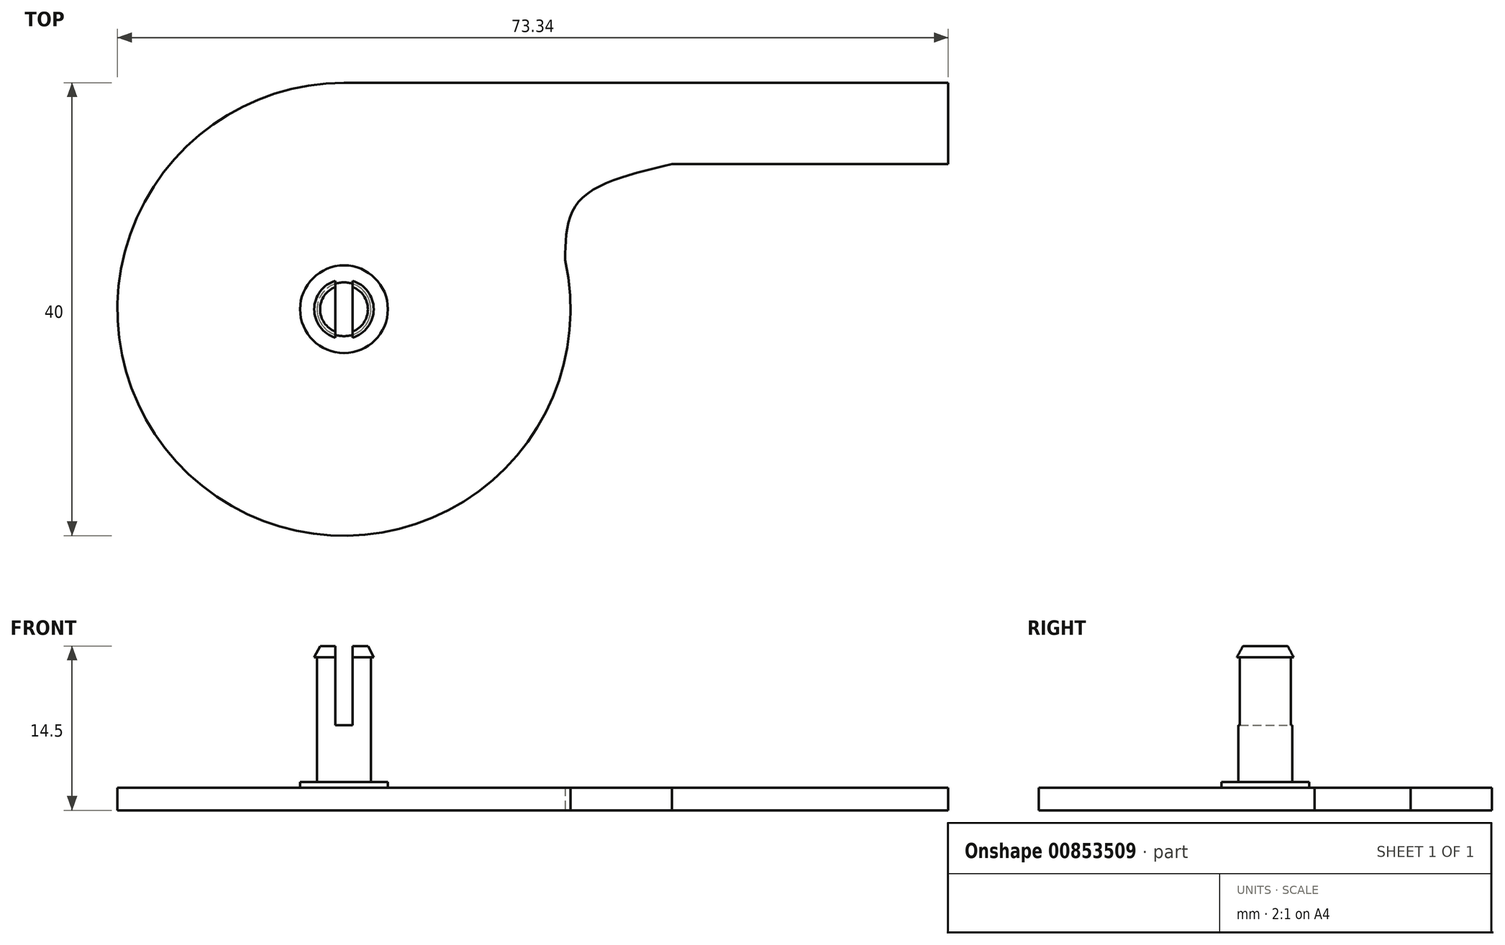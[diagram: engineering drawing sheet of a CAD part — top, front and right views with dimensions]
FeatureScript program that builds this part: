
annotation { "Feature Type Name" : "Feature", "Feature Type Description" : "" }
export const myFeature = defineFeature(function(context is Context, id is Id, definition is map)
    precondition{}
    {
        {
            var Q0;
            Q0=qCreatedBy(makeId("Top.planeOp"),FACE);
            var sketch = newSketch(context, id + "F0", { "sketchPlane" : qUnion([Q0])});
            skCircle(sketch, "E0", {"center": v(0, 0) * mm, "radius": 20 * mm});
            skLineSegment(sketch, "E1", {"start": v(0, 20) * mm, "end": v(53.34, 20) * mm});
            skLineSegment(sketch, "E2", {"start": v(53.34, 20) * mm, "end": v(53.34, 12.82) * mm});
            skLineSegment(sketch, "E3", {"start": v(53.34, 12.82) * mm, "end": v(28.94, 12.82) * mm});
            skFitSpline(sketch, "E4", {"points": [v(19.52, 4.35) * mm, v(20.72, 9.5) * mm, v(28.94, 12.82) * mm], "startDerivative": vector(0.2, 13.14) * mm, "endDerivative": vector(17.92, 4.2) * mm});
            skSolve(sketch);
        }
        {
            var Q0;
            {var subQ0=sQuery(id+"F0.wireOp",EDGE,"E0");var subQ1=makeQuery(id+"F0.imprint","INTERSECT",VERTEX,{"derivedFrom":[subQ0,sQuery(id+"F0.wireOp",EDGE,"E1")]});Q0=makeQuery(id+"F0.imprint","IMPRINT",FACE,{"disambiguationData":[TD([[makeQuery(id+"F0.imprint","IMPRINT",EDGE,{"disambiguationData":[TD([[subQ1,1.0]])],"derivedFrom":subQ0}),1.0]])]});}
            var Q1;
            {var subQ0=sQuery(id+"F0.wireOp",EDGE,"E1");Q1=makeQuery(id+"F0.imprint","IMPRINT",FACE,{"disambiguationData":[TD([[makeQuery(id+"F0.imprint","IMPRINT",EDGE,{"derivedFrom":subQ0}),-1.0]])]});}
            extrude(context, id + "F1", {"entities" : qUnion([Q0, Q1]), "depth" : 2 * mm, "offsetDistance" : 25 * mm});
        }
        {
            var Q0;
            Q0=qCreatedBy(makeId("Front.planeOp"),FACE);
            var sketch = newSketch(context, id + "F2", { "sketchPlane" : qUnion([Q0])});
            skLineSegment(sketch, "E5", {"start": v(0, 0) * mm, "end": v(-2.38, 0) * mm});
            skLineSegment(sketch, "E6", {"start": v(-2.38, 2.5) * mm, "end": v(-2.38, 13.5) * mm});
            skLineSegment(sketch, "E7", {"start": v(-2.63, 13.5) * mm, "end": v(-2.38, 13.5) * mm});
            skLineSegment(sketch, "E8", {"start": v(-2.11, 14.5) * mm, "end": v(0, 14.5) * mm});
            skLineSegment(sketch, "E9", {"start": v(-2.63, 13.5) * mm, "end": v(-2.11, 14.5) * mm});
            skPoint(sketch, "E10.orphan", {"position": v(0, 13.5) * mm});
            skLineSegment(sketch, "E11", {"start": v(0, 0) * mm, "end": v(0, 14.5) * mm});
            skLineSegment(sketch, "E12", {"start": v(0, -1.32) * mm, "end": v(0, 13.7) * mm, "construction": true});
            skLineSegment(sketch, "E13", {"start": v(-2.38, 2.5) * mm, "end": v(-3.88, 2.5) * mm});
            skLineSegment(sketch, "E14", {"start": v(-3.88, 2.5) * mm, "end": v(-3.88, 0) * mm});
            skLineSegment(sketch, "E15", {"start": v(-3.88, 0) * mm, "end": v(-2.38, 0) * mm});
            skSolve(sketch);
        }
        {
            var Q0;
            Q0=makeQuery(id+"F2.imprint","IMPRINT",FACE,{"disambiguationData":[TD([[makeQuery(id+"F2.imprint","IMPRINT",EDGE,{"derivedFrom":sQuery(id+"F2.wireOp",EDGE,"E5")}),-1.0]])]});
            var Q1;
            Q1=sQuery(id+"F2.wireOp",EDGE,"E12");
            revolve(context, id + "F3", {"operationType" : NewBodyOperationType.ADD, "surfaceOperationType" : NewSurfaceOperationType.NEW, "entities" : qUnion([Q0]), "axis" : qUnion([Q1]), "revolveType" : RevolveType.FULL});
        }
        {
            var Q0;
            Q0=makeQuery(id+"F3.opRevolve","SWEPT_FACE",FACE,{"disambiguationData":[OSD([sQuery(id+"F2.wireOp",EDGE,"E8")])]});
            var sketch = newSketch(context, id + "F4", { "sketchPlane" : qUnion([Q0])});
            skLineSegment(sketch, "E16.bottom", {"start": v(0.75, -4.46) * mm, "end": v(-0.75, -4.46) * mm});
            skLineSegment(sketch, "E16.top", {"start": v(0.75, 4.46) * mm, "end": v(-0.75, 4.46) * mm});
            skLineSegment(sketch, "E16.left", {"start": v(0.75, -4.46) * mm, "end": v(0.75, 4.46) * mm});
            skLineSegment(sketch, "E16.right", {"start": v(-0.75, -4.46) * mm, "end": v(-0.75, 4.46) * mm});
            skPoint(sketch, "E16.middle", {"position": v(0, 0) * mm});
            skSolve(sketch);
        }
        {
            var Q0;
            {var subQ0=sQuery(id+"F4.wireOp",EDGE,"E16.top");Q0=makeQuery(id+"F4.imprint","IMPRINT",FACE,{"disambiguationData":[TD([[makeQuery(id+"F4.imprint","IMPRINT",EDGE,{"derivedFrom":subQ0}),1.0]])]});}
            var Q1;
            {var subQ0=sQuery(id+"F4.wireOp",EDGE,"E16.left");var subQ1=makeQuery(id+"F3.opRevolve","SWEPT_EDGE",EDGE,{"disambiguationData":[OSD([sQuery(id+"F2.wireOp",EDGE,"E8"),sQuery(id+"F2.wireOp",EDGE,"E9")])]});var subQ2=makeQuery(id+"F4.imprint","INTERSECT",VERTEX,{"disambiguationData":[OD(0.0)],"derivedFrom":[subQ1,subQ0]});Q1=makeQuery(id+"F4.imprint","IMPRINT",FACE,{"disambiguationData":[TD([[makeQuery(id+"F4.imprint","IMPRINT",EDGE,{"disambiguationData":[TD([[subQ2,-1.0]])],"derivedFrom":subQ0}),1.0]])]});}
            var Q2;
            {var subQ0=sQuery(id+"F4.wireOp",EDGE,"E16.bottom");Q2=makeQuery(id+"F4.imprint","IMPRINT",FACE,{"disambiguationData":[TD([[makeQuery(id+"F4.imprint","IMPRINT",EDGE,{"derivedFrom":subQ0}),-1.0]])]});}
            extrude(context, id + "F5", {"entities" : qUnion([Q0, Q1, Q2]), "operationType" : NewBodyOperationType.REMOVE, "oppositeDirection" : true, "depth" : 7 * mm, "offsetDistance" : 25 * mm});
        }
    });
